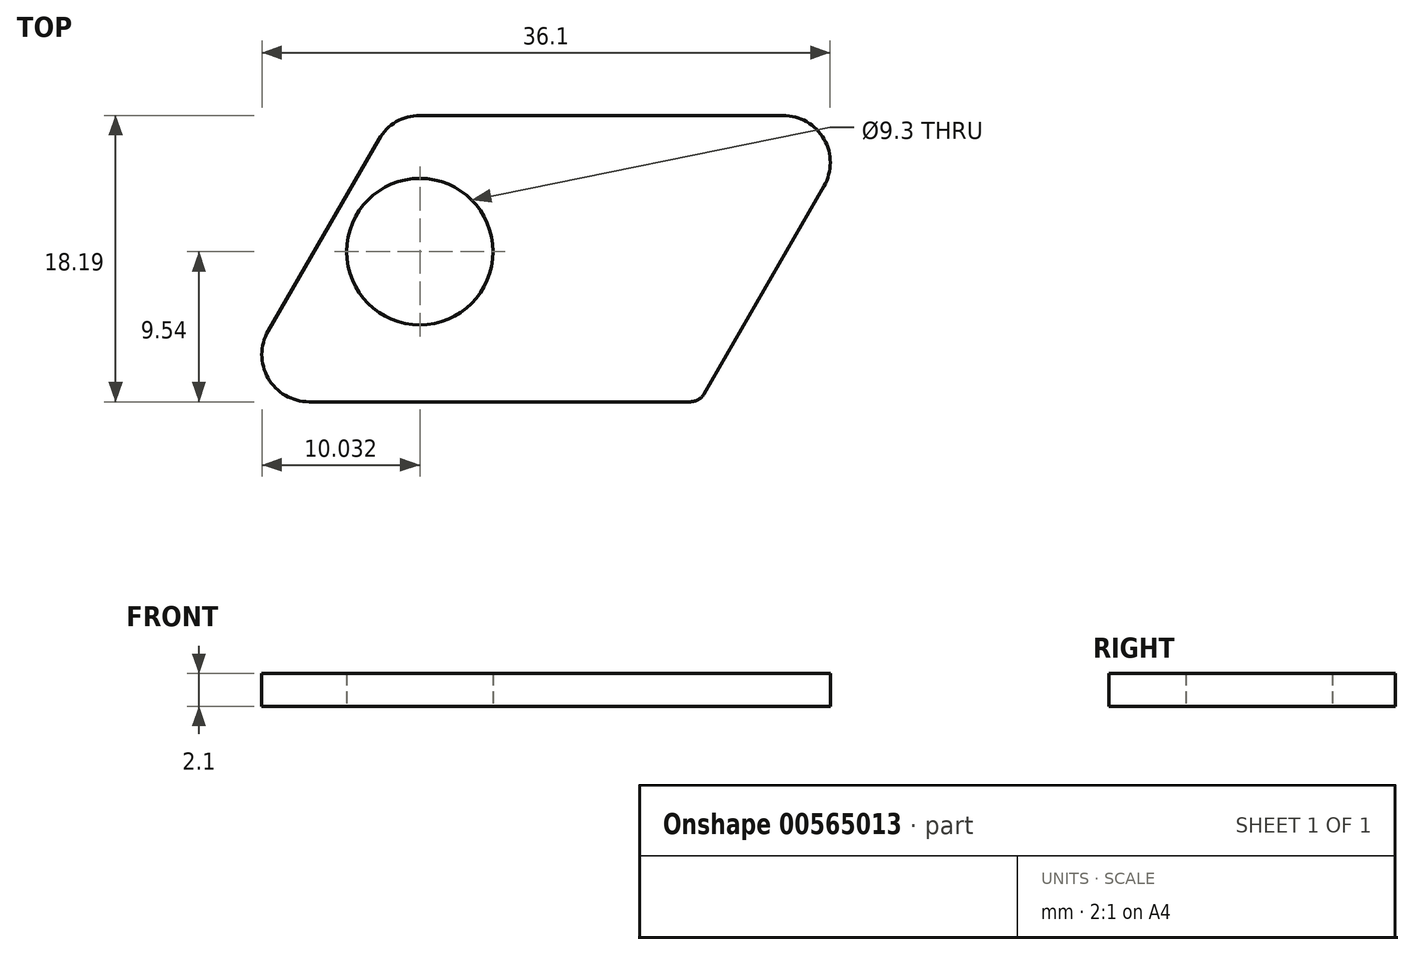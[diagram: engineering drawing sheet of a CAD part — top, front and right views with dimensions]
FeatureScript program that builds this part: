
annotation { "Feature Type Name" : "Feature", "Feature Type Description" : "" }
export const myFeature = defineFeature(function(context is Context, id is Id, definition is map)
    precondition{}
    {
        {
            var Q0;
            Q0=qCreatedBy(makeId("Top.planeOp"),FACE);
            var sketch = newSketch(context, id + "F0", { "sketchPlane" : qUnion([Q0])});
            skLineSegment(sketch, "E0", {"start": v(-5.2, 0) * mm, "end": v(-28.27, 0) * mm});
            skLineSegment(sketch, "E1", {"start": v(-2.6, -4.5) * mm, "end": v(-10.21, -17.69) * mm});
            skLineSegment(sketch, "E2", {"start": v(-30.87, -1.5) * mm, "end": v(-37.9, -13.69) * mm});
            skLineSegment(sketch, "E3", {"start": v(-35.3, -18.19) * mm, "end": v(-11.08, -18.19) * mm});
            skPoint(sketch, "E4.visualSharp", {"position": v(0, 0) * mm});
            skArc(sketch, "E4.filletArc", {"start": v(-2.6, -4.5) * mm, "mid": v(-2.6, -1.5) * mm, "end": v(-5.2, 0) * mm});
            skPoint(sketch, "E5.visualSharp", {"position": v(-40.5, -18.19) * mm});
            skArc(sketch, "E5.filletArc", {"start": v(-37.9, -13.69) * mm, "mid": v(-37.9, -16.69) * mm, "end": v(-35.3, -18.19) * mm});
            skPoint(sketch, "E6.visualSharp", {"position": v(-30, 0) * mm});
            skArc(sketch, "E6.filletArc", {"start": v(-28.27, 0) * mm, "mid": v(-29.77, -0.4) * mm, "end": v(-30.87, -1.5) * mm});
            skPoint(sketch, "E7.visualSharp", {"position": v(-10.5, -18.19) * mm});
            skArc(sketch, "E7.filletArc", {"start": v(-11.08, -18.19) * mm, "mid": v(-10.58, -18.05) * mm, "end": v(-10.21, -17.69) * mm});
            skCircle(sketch, "E8", {"center": v(-28.27, -8.65) * mm, "radius": 4.65 * mm});
            skSolve(sketch);
        }
        {
            var Q0;
            Q0=makeQuery(id+"F0.imprint","IMPRINT",FACE,{"disambiguationData":[TD([[makeQuery(id+"F0.imprint","IMPRINT",EDGE,{"derivedFrom":sQuery(id+"F0.wireOp",EDGE,"E0")}),1.0]])]});
            extrude(context, id + "F1", {"entities" : qUnion([Q0]), "depth" : 2.1 * mm, "offsetDistance" : 25 * mm});
        }
    });
